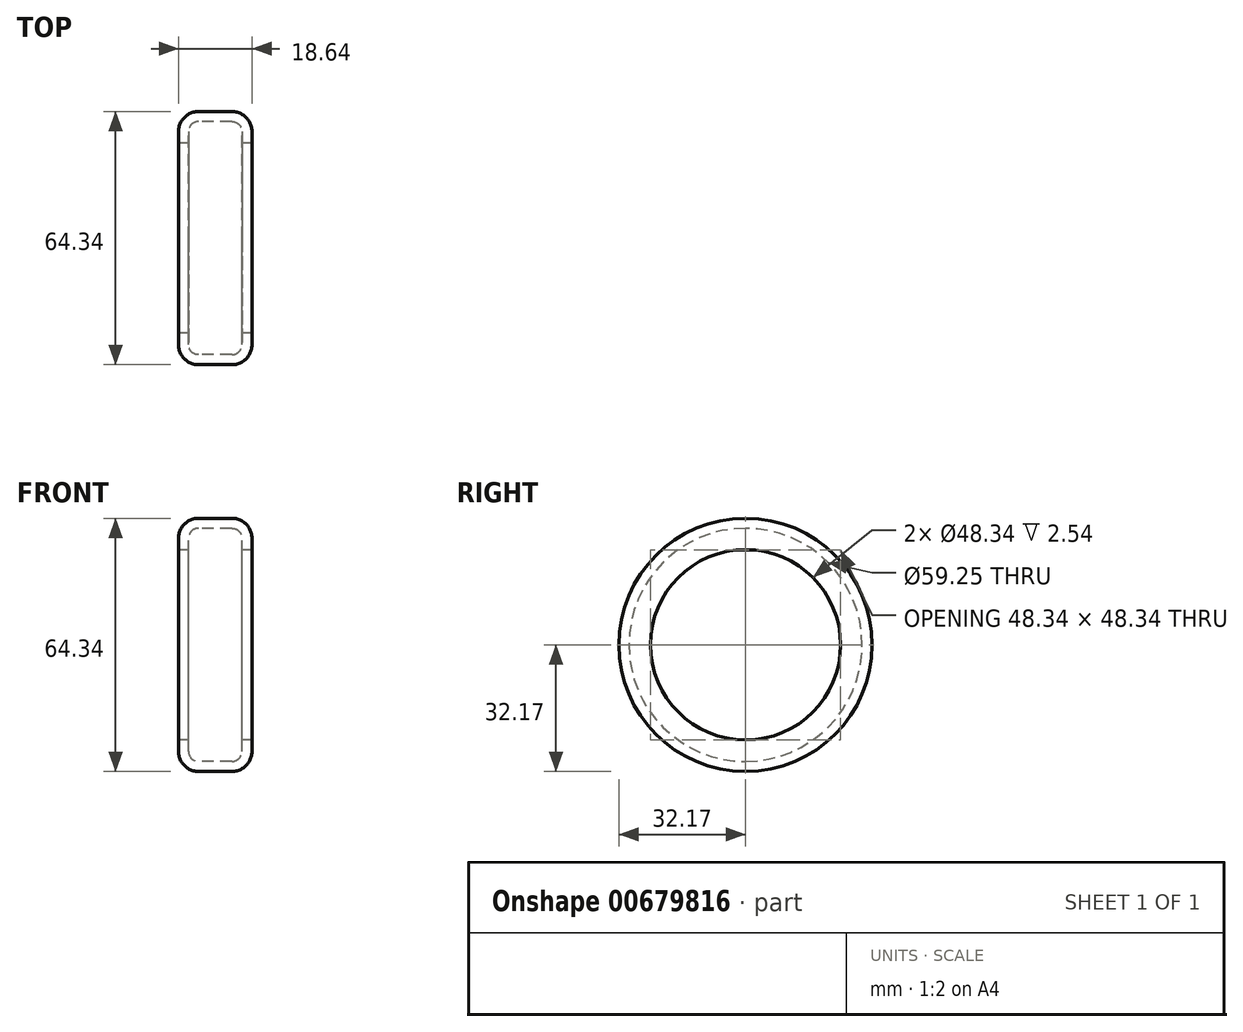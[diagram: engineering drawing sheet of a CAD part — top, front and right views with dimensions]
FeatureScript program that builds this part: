
annotation { "Feature Type Name" : "Feature", "Feature Type Description" : "" }
export const myFeature = defineFeature(function(context is Context, id is Id, definition is map)
    precondition{}
    {
        {
            var Q0;
            Q0=qCreatedBy(makeId("Front.planeOp"),FACE);
            var sketch = newSketch(context, id + "F0", { "sketchPlane" : qUnion([Q0])});
            skLineSegment(sketch, "E0", {"start": v(-20.8, 0) * mm, "end": v(22.77, 0) * mm, "construction": true});
            skLineSegment(sketch, "E1.bottom", {"start": v(-9.32, 32.17) * mm, "end": v(0, 32.17) * mm});
            skLineSegment(sketch, "E1.top", {"start": v(-9.32, 24.17) * mm, "end": v(0, 24.17) * mm});
            skLineSegment(sketch, "E1.left", {"start": v(-9.32, 32.17) * mm, "end": v(-9.32, 24.17) * mm});
            skLineSegment(sketch, "E2.MirrorCS", {"start": v(9.32, 24.17) * mm, "end": v(0, 24.17) * mm});
            skLineSegment(sketch, "E3.MirrorCS", {"start": v(9.32, 32.17) * mm, "end": v(9.32, 24.17) * mm});
            skLineSegment(sketch, "E4.MirrorCS", {"start": v(9.32, 32.17) * mm, "end": v(0, 32.17) * mm});
            skLineSegment(sketch, "E5.trimOffspring", {"start": v(0, 24.17) * mm, "end": v(0, -15.91) * mm, "construction": true});
            skPoint(sketch, "E6.start.orphan", {"position": v(0, 35.53) * mm});
            skSolve(sketch);
        }
        {
            var Q0;
            Q0=makeQuery(id+"F0.imprint","IMPRINT",FACE,{"disambiguationData":[TD([[makeQuery(id+"F0.imprint","IMPRINT",EDGE,{"derivedFrom":sQuery(id+"F0.wireOp",EDGE,"E1.bottom")}),-1.0]])]});
            var Q1;
            Q1=sQuery(id+"F0.wireOp",EDGE,"E0");
            revolve(context, id + "F1", {"entities" : qUnion([Q0]), "axis" : qUnion([Q1]), "revolveType" : RevolveType.FULL});
        }
        {
            var Q0;
            Q0=makeQuery(id+"F1.opRevolve","SWEPT_EDGE",EDGE,{"disambiguationData":[OSD([sQuery(id+"F0.wireOp",EDGE,"E3.MirrorCS"),sQuery(id+"F0.wireOp",EDGE,"E4.MirrorCS")])]});
            fillet(context, id + "F2", {"entities" : qUnion([Q0]), "radius" : 5.08 * mm, "tangentPropagation" : true, "allowEdgeOverflow" : false});
        }
        {
            var Q0;
            Q0=makeQuery(id+"F1.opRevolve","SWEPT_EDGE",EDGE,{"disambiguationData":[OSD([sQuery(id+"F0.wireOp",EDGE,"E1.bottom"),sQuery(id+"F0.wireOp",EDGE,"E1.left")])]});
            fillet(context, id + "F3", {"entities" : qUnion([Q0]), "radius" : 5.08 * mm, "tangentPropagation" : true, "allowEdgeOverflow" : false});
        }
        {
            var Q0;
            Q0=makeQuery(id+"F1.opRevolve","SWEPT_FACE",FACE,{"disambiguationData":[OSD([sQuery(id+"F0.wireOp",EDGE,"E1.top"),sQuery(id+"F0.wireOp",EDGE,"E2.MirrorCS")])]});
            shell(context, id + "F4", {"entities" : qUnion([Q0]), "thickness" : 2.54 * mm});
        }
    });
